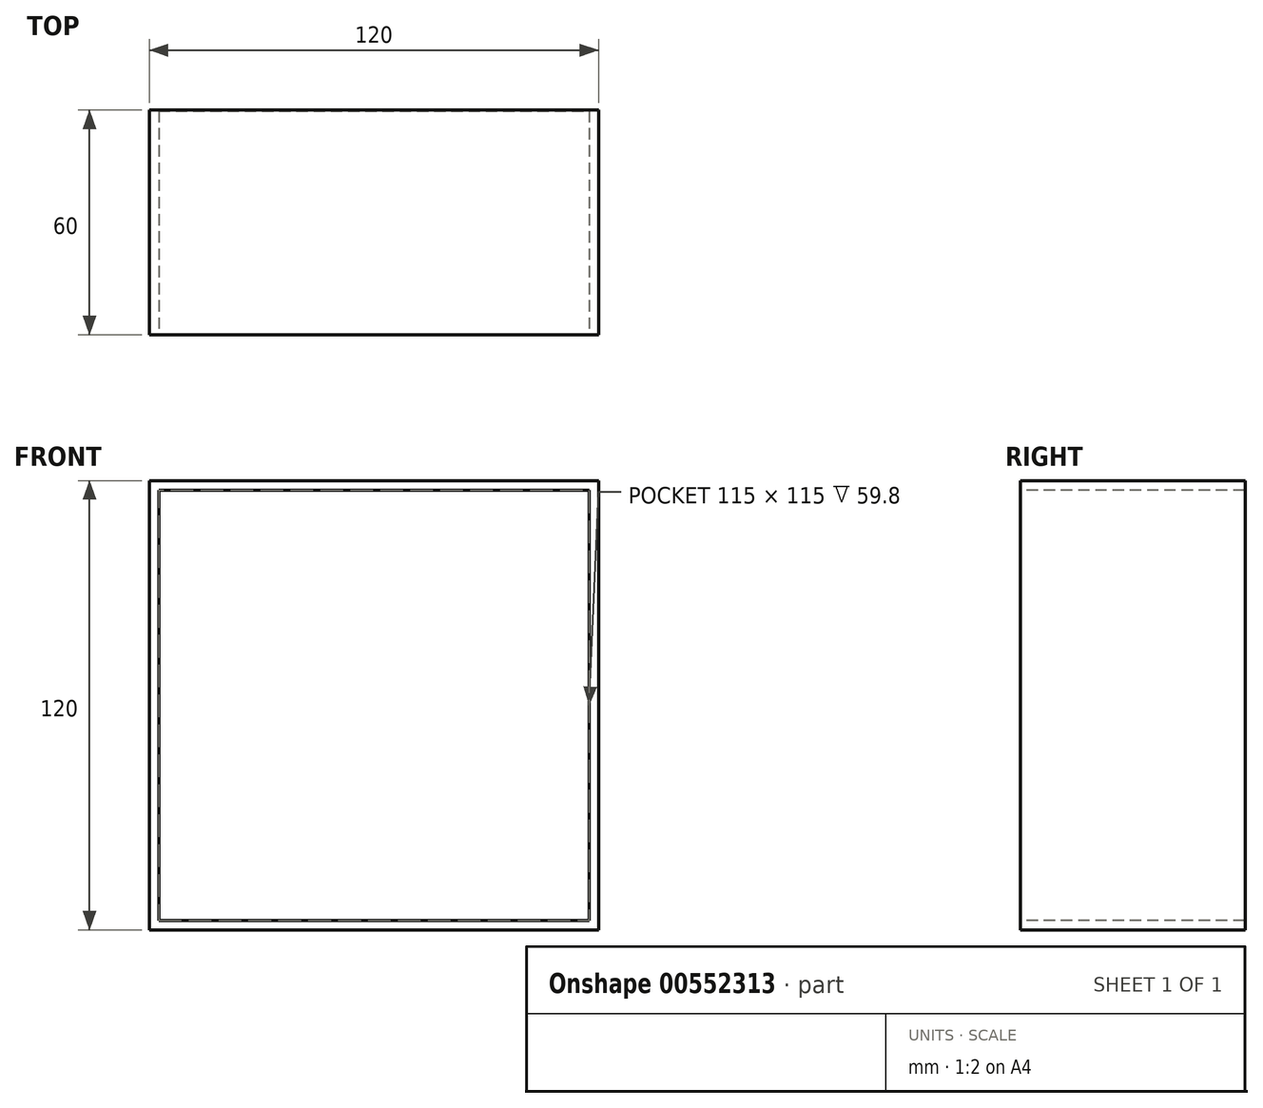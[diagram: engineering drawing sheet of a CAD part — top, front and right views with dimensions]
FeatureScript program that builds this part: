
annotation { "Feature Type Name" : "Feature", "Feature Type Description" : "" }
export const myFeature = defineFeature(function(context is Context, id is Id, definition is map)
    precondition{}
    {
        {
            var Q0;
            Q0=qCreatedBy(makeId("Front.planeOp"),FACE);
            var sketch = newSketch(context, id + "F0", { "sketchPlane" : qUnion([Q0])});
            skLineSegment(sketch, "E0.bottom", {"start": v(-60, 60) * mm, "end": v(60, 60) * mm});
            skLineSegment(sketch, "E0.top", {"start": v(-60, -60) * mm, "end": v(60, -60) * mm});
            skLineSegment(sketch, "E0.left", {"start": v(-60, 60) * mm, "end": v(-60, -60) * mm});
            skLineSegment(sketch, "E0.right", {"start": v(60, 60) * mm, "end": v(60, -60) * mm});
            skPoint(sketch, "E0.middle", {"position": v(0, 0) * mm});
            skSolve(sketch);
        }
        {
            var Q0;
            Q0=makeQuery(id+"F0.imprint","IMPRINT",FACE,{"disambiguationData":[TD([[makeQuery(id+"F0.imprint","IMPRINT",EDGE,{"derivedFrom":sQuery(id+"F0.wireOp",EDGE,"E0.bottom")}),-1.0]])]});
            extrude(context, id + "F1", {"entities" : qUnion([Q0]), "oppositeDirection" : true, "depth" : 60 * mm, "offsetDistance" : 25 * mm});
        }
        {
            var Q0;
            Q0=qCreatedBy(makeId("Front.planeOp"),FACE);
            var sketch = newSketch(context, id + "F2", { "sketchPlane" : qUnion([Q0])});
            skLineSegment(sketch, "E1.bottom", {"start": v(-57.5, 57.5) * mm, "end": v(57.5, 57.5) * mm});
            skLineSegment(sketch, "E1.top", {"start": v(-57.5, -57.5) * mm, "end": v(57.5, -57.5) * mm});
            skLineSegment(sketch, "E1.left", {"start": v(-57.5, 57.5) * mm, "end": v(-57.5, -57.5) * mm});
            skLineSegment(sketch, "E1.right", {"start": v(57.5, 57.5) * mm, "end": v(57.5, -57.5) * mm});
            skPoint(sketch, "E1.middle", {"position": v(0, 0) * mm});
            skSolve(sketch);
        }
        {
            var Q0;
            Q0=makeQuery(id+"F2.imprint","IMPRINT",FACE,{"disambiguationData":[TD([[makeQuery(id+"F2.imprint","IMPRINT",EDGE,{"derivedFrom":sQuery(id+"F2.wireOp",EDGE,"E1.bottom")}),-1.0]])]});
            extrude(context, id + "F3", {"entities" : qUnion([Q0]), "operationType" : NewBodyOperationType.REMOVE, "oppositeDirection" : true, "depth" : 59.8 * mm, "offsetDistance" : 25 * mm});
        }
        {
            var Q0;
            Q0=qCreatedBy(makeId("Front.planeOp"),FACE);
            var sketch = newSketch(context, id + "F4", { "sketchPlane" : qUnion([Q0])});
            skCircle(sketch, "E2", {"center": v(0, -1.96) * mm, "radius": 9.74 * mm});
            skSolve(sketch);
        }
        {
            var Q0;
            Q0=sQuery(id+"F4.wireOp",EDGE,"E2");
            extrude(context, id + "F5", {"bodyType" : ToolBodyType.SURFACE, "surfaceEntities" : qUnion([Q0]), "oppositeDirection" : true, "depth" : 59.4 * mm, "offsetDistance" : 25 * mm});
        }
        {
            var Q0;
            Q0=qCreatedBy(makeId("Right.planeOp"),FACE);
            var sketch = newSketch(context, id + "F6", { "sketchPlane" : qUnion([Q0])});
            skCircle(sketch, "E3", {"center": v(30.86, 0) * mm, "radius": 67.6 * mm});
            skPoint(sketch, "E3.first.point", {"position": v(0, 60.13) * mm});
            skPoint(sketch, "E3.second.point", {"position": v(0, -60.14) * mm});
            skPoint(sketch, "E3.third.point", {"position": v(-36.73, 0) * mm});
            skSolve(sketch);
        }
        {
            var Q0;
            Q0=sQuery(id+"F6.wireOp",EDGE,"E3");
            extrude(context, id + "F7", {"bodyType" : ToolBodyType.SURFACE, "surfaceEntities" : qUnion([Q0]), "depth" : 60 * mm, "offsetDistance" : 25 * mm, "hasSecondDirection" : true, "secondDirectionOppositeDirection" : true, "secondDirectionDepth" : 60 * mm});
        }
    });
